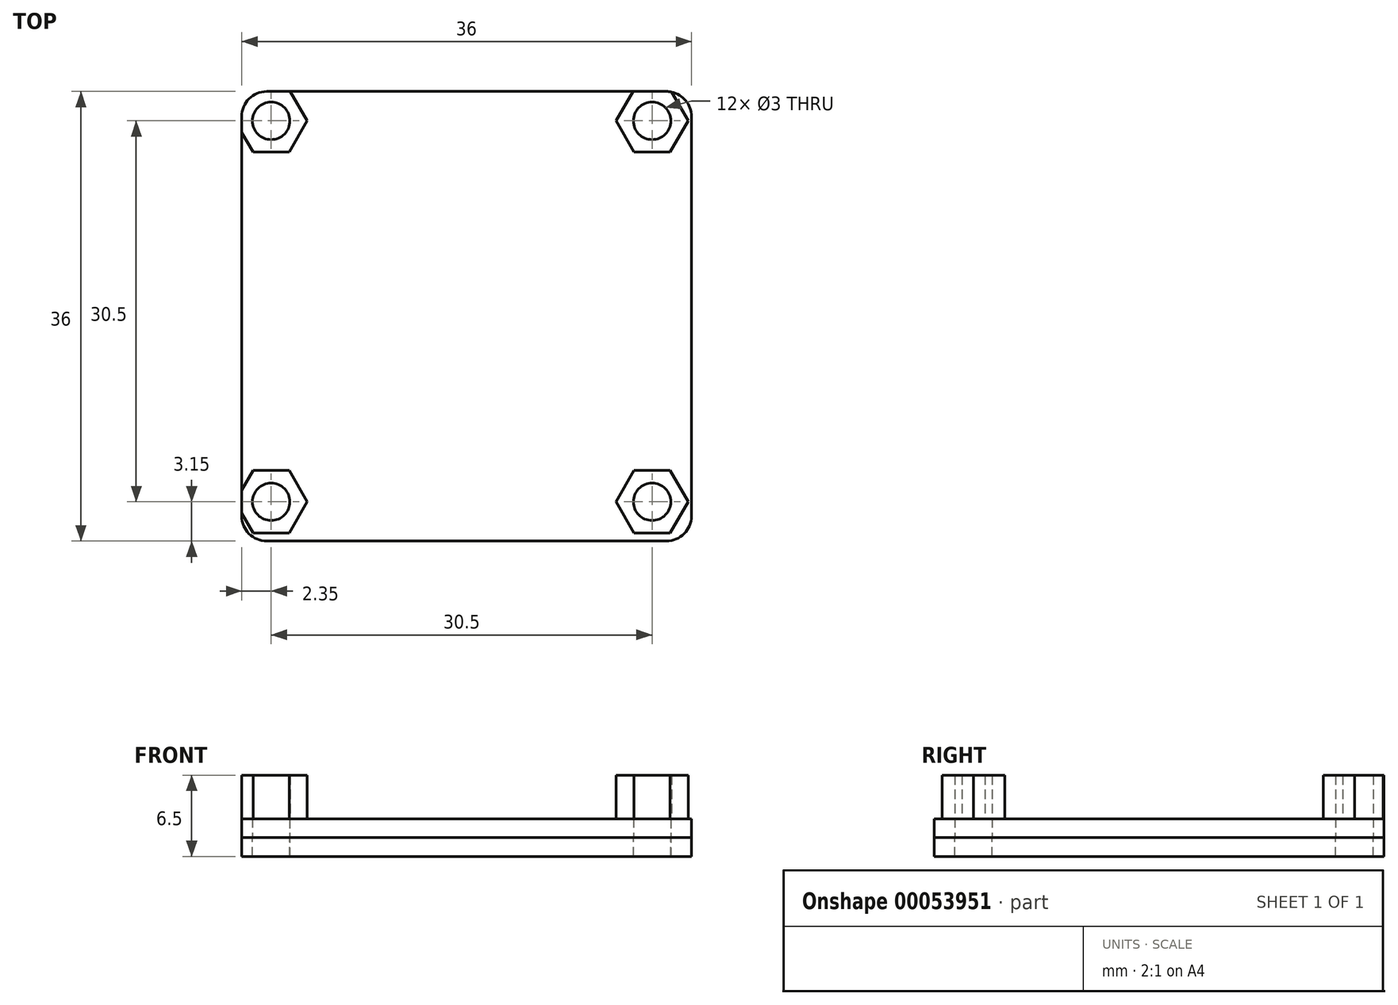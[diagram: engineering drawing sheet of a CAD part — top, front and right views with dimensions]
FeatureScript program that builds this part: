
annotation { "Feature Type Name" : "Feature", "Feature Type Description" : "" }
export const myFeature = defineFeature(function(context is Context, id is Id, definition is map)
    precondition{}
    {
        {
            var Q0;
            Q0=qCreatedBy(makeId("Top.planeOp"),FACE);
            var sketch = newSketch(context, id + "F0", { "sketchPlane" : qUnion([Q0])});
            skLineSegment(sketch, "E0.rect.bottom", {"start": v(16.4, -18.4) * mm, "end": v(-15.6, -18.4) * mm});
            skLineSegment(sketch, "E0.rect.top", {"start": v(16.4, 17.6) * mm, "end": v(-15.6, 17.6) * mm});
            skLineSegment(sketch, "E0.rect.left", {"start": v(18.4, -16.4) * mm, "end": v(18.4, 15.6) * mm});
            skLineSegment(sketch, "E0.rect.right", {"start": v(-17.6, -16.4) * mm, "end": v(-17.6, 15.6) * mm});
            skPoint(sketch, "E0.rect.middle", {"position": v(0, 0) * mm});
            skLineSegment(sketch, "E1.rect.bottom", {"start": v(15.25, -15.25) * mm, "end": v(-15.25, -15.25) * mm, "construction": true});
            skLineSegment(sketch, "E1.rect.top", {"start": v(15.25, 15.25) * mm, "end": v(-15.25, 15.25) * mm, "construction": true});
            skLineSegment(sketch, "E1.rect.left", {"start": v(15.25, -15.25) * mm, "end": v(15.25, 15.25) * mm, "construction": true});
            skLineSegment(sketch, "E1.rect.right", {"start": v(-15.25, -15.25) * mm, "end": v(-15.25, 15.25) * mm, "construction": true});
            skPoint(sketch, "E2.visualSharp", {"position": v(-17.6, 17.6) * mm});
            skArc(sketch, "E2.filletArc", {"start": v(-15.6, 17.6) * mm, "mid": v(-17.02, 17.02) * mm, "end": v(-17.6, 15.6) * mm});
            skArc(sketch, "E3.filletArc", {"start": v(18.4, 15.6) * mm, "mid": v(17.81, 17.02) * mm, "end": v(16.4, 17.6) * mm});
            skArc(sketch, "E4.filletArc", {"start": v(16.4, -18.4) * mm, "mid": v(17.81, -17.81) * mm, "end": v(18.4, -16.4) * mm});
            skArc(sketch, "E5.filletArc", {"start": v(-17.6, -16.4) * mm, "mid": v(-17.02, -17.81) * mm, "end": v(-15.6, -18.4) * mm});
            skPoint(sketch, "E6.0.midPoint", {"position": v(-15.25, 12.75) * mm});
            skPoint(sketch, "E7", {"position": v(-15.25, 15.25) * mm});
            skPoint(sketch, "E8", {"position": v(15.25, 15.25) * mm});
            skPoint(sketch, "E9", {"position": v(15.25, -15.25) * mm});
            skPoint(sketch, "E10", {"position": v(-15.25, -15.25) * mm});
            skCircle(sketch, "E11", {"center": v(-15.25, 15.25) * mm, "radius": 1.5 * mm});
            skCircle(sketch, "E12", {"center": v(15.25, 15.25) * mm, "radius": 1.5 * mm});
            skCircle(sketch, "E13", {"center": v(-15.25, -15.25) * mm, "radius": 1.5 * mm});
            skCircle(sketch, "E14", {"center": v(15.25, -15.25) * mm, "radius": 1.5 * mm});
            skSolve(sketch);
        }
        {
            var Q0;
            {var subQ0=sQuery(id+"F0.wireOp",EDGE,"067a9122-ce82-44df-8a8c-a7cc64e2cd88.5");var subQ1=sQuery(id+"F0.wireOp",EDGE,"E0.rect.left");var subQ2=makeQuery(id+"F0.imprint","INTERSECT",VERTEX,{"derivedFrom":[subQ1,subQ0]});Q0=makeQuery(id+"F0.imprint","IMPRINT",FACE,{"disambiguationData":[TD([[makeQuery(id+"F0.imprint","IMPRINT",EDGE,{"disambiguationData":[TD([[subQ2,-1.0]])],"derivedFrom":subQ1}),-1.0]])]});}
            var Q1;
            {var subQ0=sQuery(id+"F0.wireOp",EDGE,"0594f8a3-0fcc-4db6-aeb1-54b5dbc3f25d.5");var subQ1=sQuery(id+"F0.wireOp",EDGE,"E0.rect.left");var subQ2=makeQuery(id+"F0.imprint","INTERSECT",VERTEX,{"derivedFrom":[subQ1,subQ0]});Q1=makeQuery(id+"F0.imprint","IMPRINT",FACE,{"disambiguationData":[TD([[makeQuery(id+"F0.imprint","IMPRINT",EDGE,{"disambiguationData":[TD([[subQ2,-1.0]])],"derivedFrom":subQ1}),-1.0]])]});}
            var Q2;
            {var subQ0=sQuery(id+"F0.wireOp",EDGE,"93ebb783-1b2a-4d24-b839-b5876bac681c.1");var subQ1=sQuery(id+"F0.wireOp",EDGE,"E0.rect.right");var subQ2=makeQuery(id+"F0.imprint","INTERSECT",VERTEX,{"derivedFrom":[subQ1,subQ0]});Q2=makeQuery(id+"F0.imprint","IMPRINT",FACE,{"disambiguationData":[TD([[makeQuery(id+"F0.imprint","IMPRINT",EDGE,{"disambiguationData":[TD([[subQ2,-1.0]])],"derivedFrom":subQ1}),1.0]])]});}
            var Q3;
            {var subQ0=sQuery(id+"F0.wireOp",EDGE,"E6.1");var subQ1=sQuery(id+"F0.wireOp",EDGE,"E0.rect.right");var subQ2=makeQuery(id+"F0.imprint","INTERSECT",VERTEX,{"derivedFrom":[subQ1,subQ0]});Q3=makeQuery(id+"F0.imprint","IMPRINT",FACE,{"disambiguationData":[TD([[makeQuery(id+"F0.imprint","IMPRINT",EDGE,{"disambiguationData":[TD([[subQ2,-1.0]])],"derivedFrom":subQ1}),1.0]])]});}
            var Q4;
            Q4=makeQuery(id+"F0.imprint","IMPRINT",FACE,{"disambiguationData":[TD([[makeQuery(id+"F0.imprint","IMPRINT",EDGE,{"derivedFrom":sQuery(id+"F0.wireOp",EDGE,"E0.rect.bottom")}),-1.0]])]});
            extrude(context, id + "F1", {"entities" : qUnion([Q0, Q1, Q2, Q3, Q4]), "depth" : 1.5 * mm});
        }
        {
            var Q0;
            Q0=makeQuery(id+"F1.opExtrude","CAP_FACE",FACE,{"disambiguationData":[OSD([sQuery(id+"F0.wireOp",EDGE,"E0.rect.bottom"),sQuery(id+"F0.wireOp",EDGE,"E0.rect.top"),sQuery(id+"F0.wireOp",EDGE,"E0.rect.left"),sQuery(id+"F0.wireOp",EDGE,"E0.rect.right"),sQuery(id+"F0.wireOp",EDGE,"E2.filletArc"),sQuery(id+"F0.wireOp",EDGE,"E3.filletArc"),sQuery(id+"F0.wireOp",EDGE,"E4.filletArc"),sQuery(id+"F0.wireOp",EDGE,"E5.filletArc")])],"isStart":false});
            var sketch = newSketch(context, id + "F2", { "sketchPlane" : qUnion([Q0])});
            skLineSegment(sketch, "E15.rect.bottom", {"start": v(-15.25, 15.25) * mm, "end": v(15.25, 15.25) * mm});
            skLineSegment(sketch, "E15.rect.top", {"start": v(-15.25, -15.25) * mm, "end": v(15.25, -15.25) * mm});
            skLineSegment(sketch, "E15.rect.left", {"start": v(-15.25, 15.25) * mm, "end": v(-15.25, -15.25) * mm});
            skLineSegment(sketch, "E15.rect.right", {"start": v(15.25, 15.25) * mm, "end": v(15.25, -15.25) * mm});
            skPoint(sketch, "E15.rect.middle", {"position": v(0, 0) * mm});
            skCircle(sketch, "E16.cCircle", {"center": v(-15.25, 15.25) * mm, "radius": 2.5 * mm, "construction": true});
            skLineSegment(sketch, "E16.0", {"start": v(-13.8, 12.75) * mm, "end": v(-16.7, 12.75) * mm});
            skLineSegment(sketch, "E16.1", {"start": v(-16.7, 12.75) * mm, "end": v(-18.14, 15.25) * mm});
            skLineSegment(sketch, "E16.2", {"start": v(-18.14, 15.25) * mm, "end": v(-16.7, 17.75) * mm});
            skLineSegment(sketch, "E16.3", {"start": v(-16.7, 17.75) * mm, "end": v(-13.8, 17.75) * mm});
            skLineSegment(sketch, "E16.4", {"start": v(-13.8, 17.75) * mm, "end": v(-12.36, 15.25) * mm});
            skLineSegment(sketch, "E16.5", {"start": v(-12.36, 15.25) * mm, "end": v(-13.8, 12.75) * mm});
            skPoint(sketch, "E16.0.midPoint", {"position": v(-15.25, 12.75) * mm});
            skCircle(sketch, "E17.cCircle", {"center": v(15.25, 15.25) * mm, "radius": 2.5 * mm, "construction": true});
            skLineSegment(sketch, "E17.0", {"start": v(16.7, 12.75) * mm, "end": v(13.8, 12.75) * mm});
            skLineSegment(sketch, "E17.1", {"start": v(13.8, 12.75) * mm, "end": v(12.36, 15.25) * mm});
            skLineSegment(sketch, "E17.2", {"start": v(12.36, 15.25) * mm, "end": v(13.8, 17.75) * mm});
            skLineSegment(sketch, "E17.3", {"start": v(13.8, 17.75) * mm, "end": v(16.7, 17.75) * mm});
            skLineSegment(sketch, "E17.4", {"start": v(16.7, 17.75) * mm, "end": v(18.14, 15.25) * mm});
            skLineSegment(sketch, "E17.5", {"start": v(18.14, 15.25) * mm, "end": v(16.7, 12.75) * mm});
            skPoint(sketch, "E17.0.midPoint", {"position": v(15.25, 12.75) * mm});
            skCircle(sketch, "E18.cCircle", {"center": v(-15.25, -15.25) * mm, "radius": 2.5 * mm, "construction": true});
            skLineSegment(sketch, "E18.0", {"start": v(-16.7, -12.75) * mm, "end": v(-13.8, -12.75) * mm});
            skLineSegment(sketch, "E18.1", {"start": v(-13.8, -12.75) * mm, "end": v(-12.36, -15.25) * mm});
            skLineSegment(sketch, "E18.2", {"start": v(-12.36, -15.25) * mm, "end": v(-13.8, -17.75) * mm});
            skLineSegment(sketch, "E18.3", {"start": v(-13.8, -17.75) * mm, "end": v(-16.7, -17.75) * mm});
            skLineSegment(sketch, "E18.4", {"start": v(-16.7, -17.75) * mm, "end": v(-18.14, -15.25) * mm});
            skLineSegment(sketch, "E18.5", {"start": v(-18.14, -15.25) * mm, "end": v(-16.7, -12.75) * mm});
            skPoint(sketch, "E18.0.midPoint", {"position": v(-15.25, -12.75) * mm});
            skCircle(sketch, "E19.cCircle", {"center": v(15.25, -15.25) * mm, "radius": 2.5 * mm, "construction": true});
            skLineSegment(sketch, "E19.0", {"start": v(13.8, -12.75) * mm, "end": v(16.7, -12.75) * mm});
            skLineSegment(sketch, "E19.1", {"start": v(16.7, -12.75) * mm, "end": v(18.14, -15.25) * mm});
            skLineSegment(sketch, "E19.2", {"start": v(18.14, -15.25) * mm, "end": v(16.7, -17.75) * mm});
            skLineSegment(sketch, "E19.3", {"start": v(16.7, -17.75) * mm, "end": v(13.8, -17.75) * mm});
            skLineSegment(sketch, "E19.4", {"start": v(13.8, -17.75) * mm, "end": v(12.36, -15.25) * mm});
            skLineSegment(sketch, "E19.5", {"start": v(12.36, -15.25) * mm, "end": v(13.8, -12.75) * mm});
            skPoint(sketch, "E19.0.midPoint", {"position": v(15.25, -12.75) * mm});
            skSolve(sketch);
        }
        {
            var Q0;
            {var subQ0=sQuery(id+"F2.wireOp",EDGE,"E17.1");Q0=makeQuery(id+"F2.imprint","IMPRINT",FACE,{"disambiguationData":[TD([[makeQuery(id+"F2.imprint","IMPRINT",EDGE,{"derivedFrom":subQ0}),-1.0]])]});}
            var Q1;
            {var subQ0=sQuery(id+"F2.wireOp",EDGE,"E17.5");Q1=makeQuery(id+"F2.imprint","IMPRINT",FACE,{"disambiguationData":[TD([[makeQuery(id+"F2.imprint","IMPRINT",EDGE,{"derivedFrom":subQ0}),-1.0]])]});}
            var Q2;
            {var subQ0=sQuery(id+"F2.wireOp",EDGE,"E19.5");Q2=makeQuery(id+"F2.imprint","IMPRINT",FACE,{"disambiguationData":[TD([[makeQuery(id+"F2.imprint","IMPRINT",EDGE,{"derivedFrom":subQ0}),-1.0]])]});}
            var Q3;
            {var subQ0=sQuery(id+"F2.wireOp",EDGE,"E19.1");Q3=makeQuery(id+"F2.imprint","IMPRINT",FACE,{"disambiguationData":[TD([[makeQuery(id+"F2.imprint","IMPRINT",EDGE,{"derivedFrom":subQ0}),-1.0]])]});}
            var Q4;
            {var subQ0=sQuery(id+"F2.wireOp",EDGE,"E18.1");Q4=makeQuery(id+"F2.imprint","IMPRINT",FACE,{"disambiguationData":[TD([[makeQuery(id+"F2.imprint","IMPRINT",EDGE,{"derivedFrom":subQ0}),-1.0]])]});}
            var Q5;
            {var subQ0=sQuery(id+"F2.wireOp",EDGE,"E18.2");Q5=makeQuery(id+"F2.imprint","IMPRINT",FACE,{"disambiguationData":[TD([[makeQuery(id+"F2.imprint","IMPRINT",EDGE,{"derivedFrom":subQ0}),-1.0]])]});}
            var Q6;
            {var subQ0=sQuery(id+"F2.wireOp",EDGE,"E16.5");Q6=makeQuery(id+"F2.imprint","IMPRINT",FACE,{"disambiguationData":[TD([[makeQuery(id+"F2.imprint","IMPRINT",EDGE,{"derivedFrom":subQ0}),-1.0]])]});}
            var Q7;
            {var subQ7=makeQuery(id+"F1.opExtrude","CAP_EDGE",EDGE,{"disambiguationData":[OSD([sQuery(id+"F0.wireOp",EDGE,"E2.filletArc")])],"isStart":false});Q7=makeQuery(id+"F2.imprint","IMPRINT",FACE,{"disambiguationData":[TD([[makeQuery(id+"F2.imprint","IMPRINT",EDGE,{"derivedFrom":subQ7}),1.0]])]});}
            extrude(context, id + "F3", {"entities" : qUnion([Q0, Q1, Q2, Q3, Q4, Q5, Q6, Q7]), "operationType" : NewBodyOperationType.ADD, "depth" : 3.5 * mm});
        }
        {
            var Q0;
            Q0 = qSketchRegion(id + "F0", true);
            var Q1;
            Q1=makeQuery(id+"F0.imprint","IMPRINT",FACE,{"disambiguationData":[TD([[makeQuery(id+"F0.imprint","IMPRINT",EDGE,{"derivedFrom":sQuery(id+"F0.wireOp",EDGE,"E0.rect.bottom")}),-1.0]])]});
            extrude(context, id + "F4", {"entities" : qUnion([Q0, Q1]), "operationType" : NewBodyOperationType.ADD, "depth" : 1.5 * mm});
        }
        {
            var Q0;
            Q0=makeQuery(id+"F0.imprint","IMPRINT",FACE,{"disambiguationData":[TD([[makeQuery(id+"F0.imprint","IMPRINT",EDGE,{"derivedFrom":sQuery(id+"F0.wireOp",EDGE,"E0.rect.bottom")}),-1.0]])]});
            extrude(context, id + "F5", {"entities" : qUnion([Q0]), "oppositeDirection" : true, "depth" : 1.5 * mm});
        }
        {
            var Q0;
            Q0=makeQuery(id+"F0.imprint","IMPRINT",FACE,{"disambiguationData":[TD([[makeQuery(id+"F0.imprint","IMPRINT",EDGE,{"derivedFrom":sQuery(id+"F0.wireOp",EDGE,"E0.rect.bottom")}),-1.0]])]});
            extrude(context, id + "F6", {"entities" : qUnion([Q0]), "depth" : 1.5 * mm, "hasSecondDirection" : true, "secondDirectionOppositeDirection" : true, "secondDirectionDepth" : 1.5 * mm});
        }
    });
